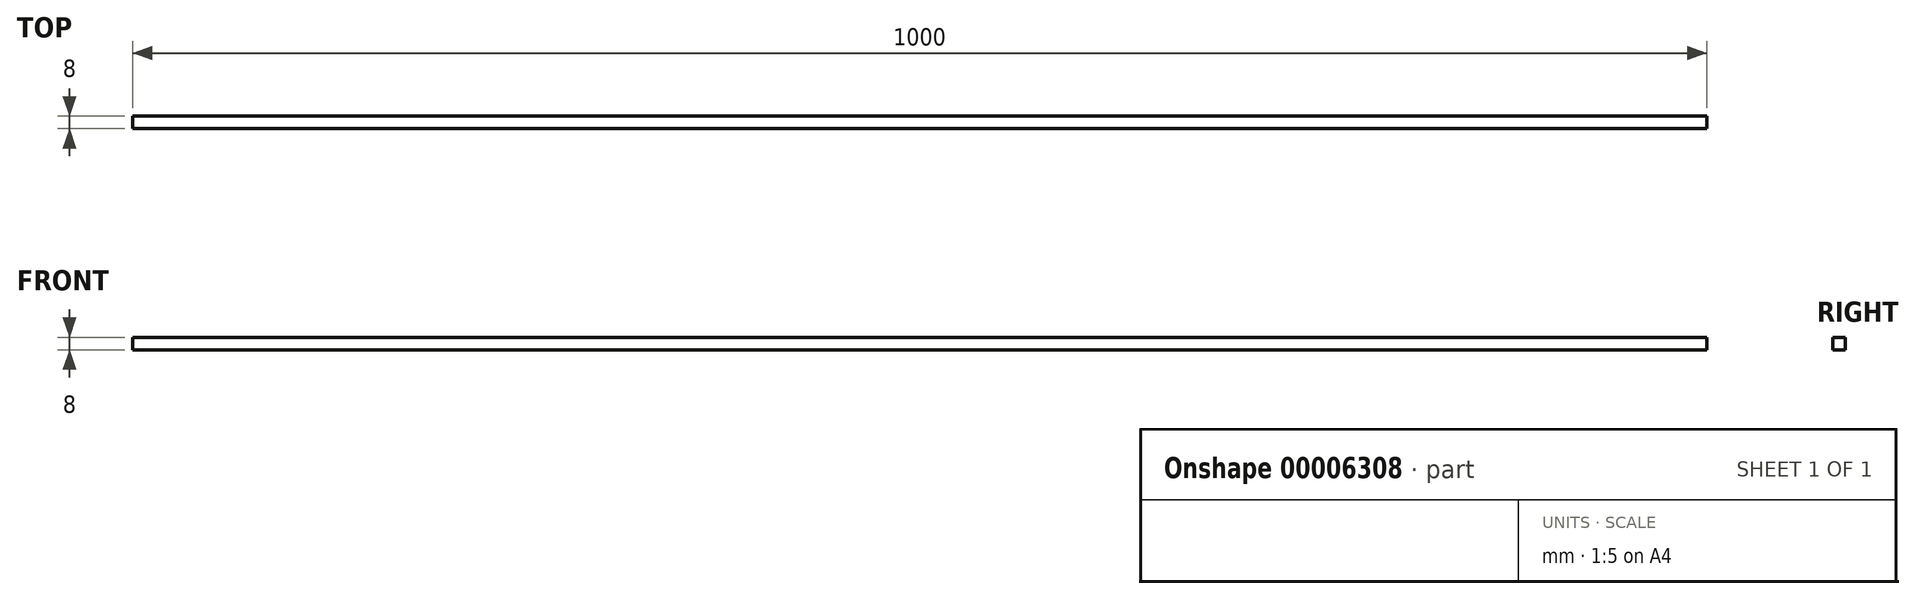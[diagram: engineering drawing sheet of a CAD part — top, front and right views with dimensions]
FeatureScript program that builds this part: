
annotation { "Feature Type Name" : "Feature", "Feature Type Description" : "" }
export const myFeature = defineFeature(function(context is Context, id is Id, definition is map)
    precondition{}
    {
        {
            var Q0;
            Q0=qCreatedBy(makeId("Right.planeOp"),FACE);
            var sketch = newSketch(context, id + "F0", { "sketchPlane" : qUnion([Q0])});
            skLineSegment(sketch, "E0.bottom", {"start": v(-3.5, 2.74) * mm, "end": v(4.5, 2.74) * mm});
            skLineSegment(sketch, "E0.top", {"start": v(-3.5, -5.26) * mm, "end": v(4.5, -5.26) * mm});
            skLineSegment(sketch, "E0.left", {"start": v(-3.5, 2.74) * mm, "end": v(-3.5, -5.26) * mm});
            skLineSegment(sketch, "E0.right", {"start": v(4.5, 2.74) * mm, "end": v(4.5, -5.26) * mm});
            skSolve(sketch);
        }
        {
            var Q0;
            Q0=makeQuery(id+"F0.imprint","IMPRINT",FACE,{"disambiguationData":[TD([[makeQuery(id+"F0.imprint","IMPRINT",EDGE,{"derivedFrom":sQuery(id+"F0.wireOp",EDGE,"E0.bottom")}),-1.0]])]});
            extrude(context, id + "F1", {"entities" : qUnion([Q0]), "oppositeDirection" : true, "depth" : 1000 * mm});
        }
    });
